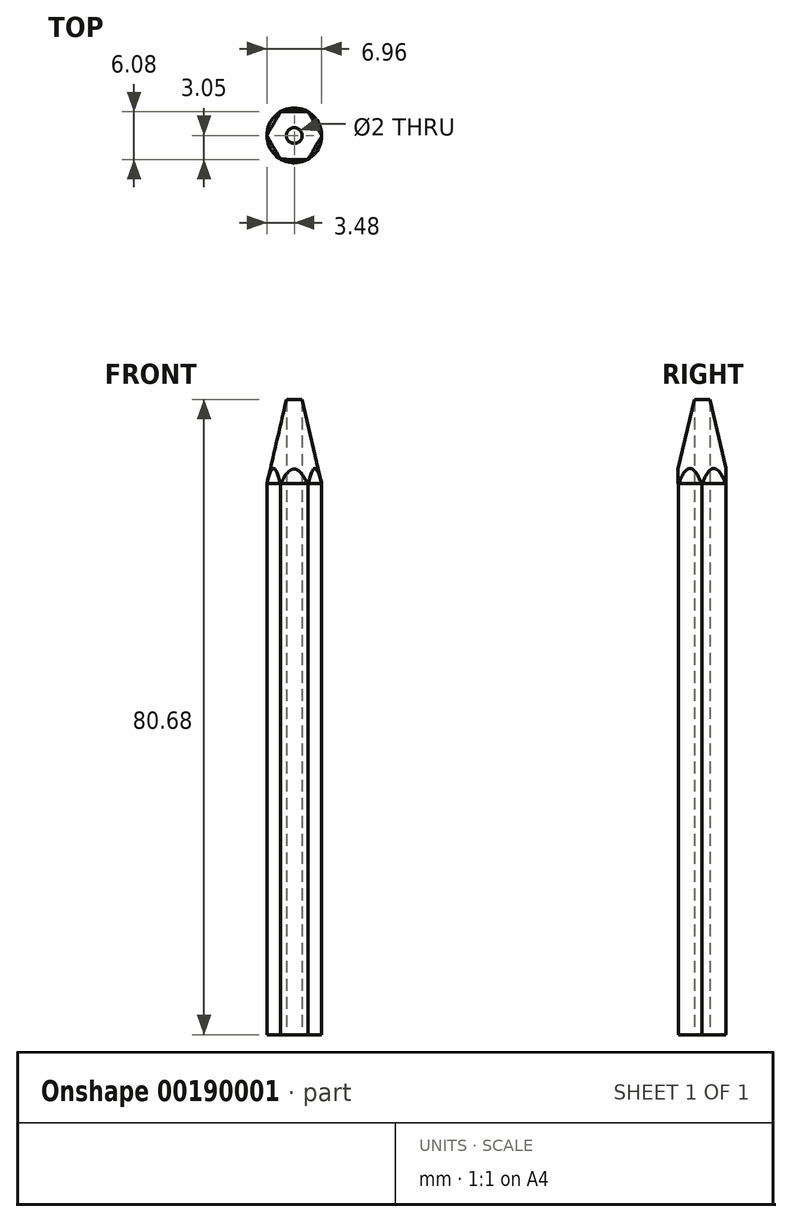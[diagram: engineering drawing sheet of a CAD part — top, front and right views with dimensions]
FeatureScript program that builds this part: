
annotation { "Feature Type Name" : "Feature", "Feature Type Description" : "" }
export const myFeature = defineFeature(function(context is Context, id is Id, definition is map)
    precondition{}
    {
        {
            var Q0;
            Q0=qCreatedBy(makeId("Top.planeOp"),FACE);
            var sketch = newSketch(context, id + "F0", { "sketchPlane" : qUnion([Q0])});
            skCircle(sketch, "E0.cCircle", {"center": v(0, 0) * mm, "radius": 3.01 * mm, "construction": true});
            skLineSegment(sketch, "E0.0", {"start": v(-3.48, 0.02) * mm, "end": v(-1.72, 3.02) * mm});
            skLineSegment(sketch, "E0.1", {"start": v(-1.72, 3.02) * mm, "end": v(1.76, 3) * mm});
            skLineSegment(sketch, "E0.2", {"start": v(1.76, 3) * mm, "end": v(3.48, -0.04) * mm});
            skLineSegment(sketch, "E0.3", {"start": v(3.48, -0.04) * mm, "end": v(1.72, -3.04) * mm});
            skLineSegment(sketch, "E0.4", {"start": v(1.72, -3.04) * mm, "end": v(-1.76, -3) * mm});
            skLineSegment(sketch, "E0.5", {"start": v(-1.76, -3) * mm, "end": v(-3.48, 0.02) * mm});
            skPoint(sketch, "E0.0.midPoint", {"position": v(-2.6, 1.52) * mm});
            skSolve(sketch);
        }
        {
            var Q0;
            Q0=makeQuery(id+"F0.imprint","IMPRINT",FACE,{"disambiguationData":[TD([[makeQuery(id+"F0.imprint","IMPRINT",EDGE,{"derivedFrom":sQuery(id+"F0.wireOp",EDGE,"E0.0")}),-1.0]])]});
            extrude(context, id + "F1", {"entities" : qUnion([Q0]), "depth" : 70 * mm});
        }
        {
            var Q0;
            Q0=qCreatedBy(makeId("Front.planeOp"),FACE);
            var sketch = newSketch(context, id + "F2", { "sketchPlane" : qUnion([Q0])});
            skLineSegment(sketch, "E1", {"start": v(0, 70) * mm, "end": v(0, 85) * mm});
            skLineSegment(sketch, "E2", {"start": v(0, 85) * mm, "end": v(-3.48, 70) * mm});
            skLineSegment(sketch, "E3", {"start": v(-3.48, 70) * mm, "end": v(0, 70) * mm});
            skSolve(sketch);
        }
        {
            var Q0;
            Q0=qCreatedBy(makeId("Top.planeOp"),FACE);
            var sketch = newSketch(context, id + "F3", { "sketchPlane" : qUnion([Q0])});
            skCircle(sketch, "E4.cCircle", {"center": v(0, 0) * mm, "radius": 3.03 * mm, "construction": true});
            skLineSegment(sketch, "E4.0", {"start": v(-3.5, 0.02) * mm, "end": v(-1.73, 3.03) * mm});
            skLineSegment(sketch, "E4.1", {"start": v(-1.73, 3.03) * mm, "end": v(1.77, 3) * mm});
            skLineSegment(sketch, "E4.2", {"start": v(1.77, 3) * mm, "end": v(3.5, -0.04) * mm});
            skLineSegment(sketch, "E4.3", {"start": v(3.5, -0.04) * mm, "end": v(1.73, -3.05) * mm});
            skLineSegment(sketch, "E4.4", {"start": v(1.73, -3.05) * mm, "end": v(-1.77, -3.03) * mm});
            skLineSegment(sketch, "E4.5", {"start": v(-1.77, -3.03) * mm, "end": v(-3.5, 0.02) * mm});
            skPoint(sketch, "E4.0.midPoint", {"position": v(-2.61, 1.53) * mm});
            skCircle(sketch, "E5", {"center": v(0, 0) * mm, "radius": 9.1 * mm});
            skSolve(sketch);
        }
        {
            var Q0;
            Q0 = qSketchRegion(id + "F2", true);
            var Q1;
            Q1=sQuery(id+"F2.wireOp",EDGE,"E1");
            revolve(context, id + "F4", {"operationType" : NewBodyOperationType.ADD, "entities" : qUnion([Q0]), "axis" : qUnion([Q1]), "revolveType" : RevolveType.FULL});
        }
        {
            var Q0;
            Q0 = qSketchRegion(id + "F3", true);
            extrude(context, id + "F5", {"entities" : qUnion([Q0]), "operationType" : NewBodyOperationType.REMOVE, "endBound" : BoundingType.THROUGH_ALL, "depth" : 25 * mm});
        }
        {
            var Q0;
            Q0=qCreatedBy(makeId("Top.planeOp"),FACE);
            var sketch = newSketch(context, id + "F6", { "sketchPlane" : qUnion([Q0])});
            skCircle(sketch, "E6", {"center": v(0, 0) * mm, "radius": 1 * mm});
            skSolve(sketch);
        }
        {
            var Q0;
            Q0 = qSketchRegion(id + "F6", true);
            extrude(context, id + "F7", {"entities" : qUnion([Q0]), "operationType" : NewBodyOperationType.REMOVE, "endBound" : BoundingType.THROUGH_ALL, "depth" : 25 * mm});
        }
    });
